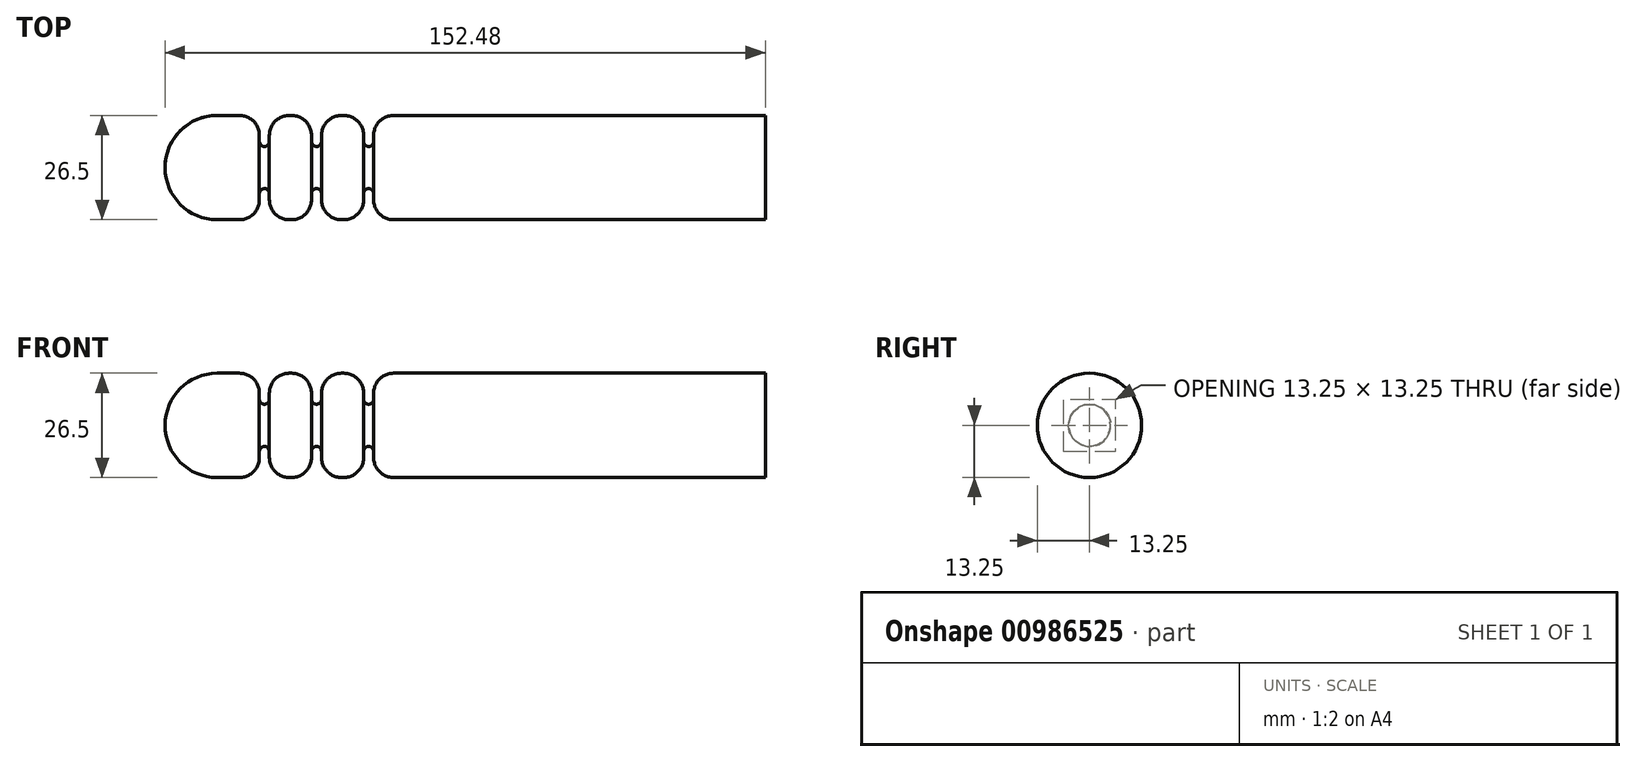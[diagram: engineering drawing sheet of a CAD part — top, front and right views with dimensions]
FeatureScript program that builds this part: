
annotation { "Feature Type Name" : "Feature", "Feature Type Description" : "" }
export const myFeature = defineFeature(function(context is Context, id is Id, definition is map)
    precondition{}
    {
        {
            var Q0;
            Q0=qCreatedBy(makeId("Top.planeOp"),FACE);
            var sketch = newSketch(context, id + "F0", { "sketchPlane" : qUnion([Q0])});
            skLineSegment(sketch, "E0", {"start": v(-75.98, 0) * mm, "end": v(76.5, 0) * mm, "construction": true});
            skCircle(sketch, "E1", {"center": v(-62.74, 0) * mm, "radius": 13.25 * mm, "construction": true});
            skCircle(sketch, "E2", {"center": v(-49.49, 0) * mm, "radius": 13.25 * mm, "construction": true});
            skLineSegment(sketch, "E3", {"start": v(-62.74, 0) * mm, "end": v(-62.74, 31.04) * mm, "construction": true});
            skLineSegment(sketch, "E4", {"start": v(-62.74, 31.04) * mm, "end": v(-62.74, 13.25) * mm, "construction": true});
            skLineSegment(sketch, "E5", {"start": v(-62.74, 13.25) * mm, "end": v(75.2, 13.25) * mm, "construction": true});
            skCircle(sketch, "E6", {"center": v(-36.24, 0) * mm, "radius": 13.25 * mm, "construction": true});
            skCircle(sketch, "E7", {"center": v(-22.99, 0) * mm, "radius": 13.25 * mm, "construction": true});
            skLineSegment(sketch, "E8", {"start": v(-49.49, 13.25) * mm, "end": v(-49.49, 0) * mm, "construction": true});
            skLineSegment(sketch, "E9", {"start": v(-36.24, 13.25) * mm, "end": v(-36.24, 0) * mm, "construction": true});
            skLineSegment(sketch, "E10", {"start": v(-22.99, 13.25) * mm, "end": v(-22.99, 0) * mm, "construction": true});
            skArc(sketch, "E11", {"start": v(-62.74, 13.25) * mm, "mid": v(-72.1, 9.37) * mm, "end": v(-75.98, 0) * mm});
            skLineSegment(sketch, "E12.0", {"start": v(-52.03, 13.25) * mm, "end": v(-52.03, 0) * mm, "construction": true});
            skLineSegment(sketch, "E13", {"start": v(-62.74, 5.36) * mm, "end": v(-3.86, 5.36) * mm, "construction": true});
            skLineSegment(sketch, "E14", {"start": v(-3.86, 5.36) * mm, "end": v(-4.4, 5.5) * mm, "construction": true});
            skLineSegment(sketch, "E15.0", {"start": v(-38.78, 13.25) * mm, "end": v(-38.78, 0) * mm, "construction": true});
            skLineSegment(sketch, "E16.0", {"start": v(-25.53, 13.25) * mm, "end": v(-25.53, 0) * mm, "construction": true});
            skLineSegment(sketch, "E17", {"start": v(-62.74, 13.25) * mm, "end": v(-52.03, 13.25) * mm});
            skLineSegment(sketch, "E18", {"start": v(-52.03, 5.36) * mm, "end": v(-52.03, 13.25) * mm});
            skLineSegment(sketch, "E19", {"start": v(-52.03, 5.36) * mm, "end": v(-49.49, 5.36) * mm});
            skLineSegment(sketch, "E20", {"start": v(-38.78, 5.36) * mm, "end": v(-38.78, 13.25) * mm});
            skLineSegment(sketch, "E21", {"start": v(-38.78, 13.25) * mm, "end": v(-49.49, 13.25) * mm});
            skLineSegment(sketch, "E22", {"start": v(-49.49, 13.25) * mm, "end": v(-49.49, 5.36) * mm});
            skLineSegment(sketch, "E23", {"start": v(-38.78, 5.36) * mm, "end": v(-36.24, 5.36) * mm});
            skLineSegment(sketch, "E24", {"start": v(-36.24, 13.25) * mm, "end": v(-36.24, 5.36) * mm});
            skLineSegment(sketch, "E25", {"start": v(-36.24, 13.25) * mm, "end": v(-25.53, 13.25) * mm});
            skLineSegment(sketch, "E26", {"start": v(-25.53, 13.25) * mm, "end": v(-25.53, 5.36) * mm});
            skLineSegment(sketch, "E27", {"start": v(-22.99, 5.36) * mm, "end": v(-25.53, 5.36) * mm});
            skLineSegment(sketch, "E28", {"start": v(-22.99, 5.36) * mm, "end": v(-22.99, 13.25) * mm});
            skLineSegment(sketch, "E29", {"start": v(-22.99, 13.25) * mm, "end": v(76.5, 13.25) * mm});
            skLineSegment(sketch, "E30", {"start": v(76.5, 0) * mm, "end": v(76.5, 13.25) * mm});
            skLineSegment(sketch, "E31", {"start": v(76.5, 0) * mm, "end": v(-75.98, 0) * mm});
            skSolve(sketch);
        }
        {
            var Q0;
            Q0=makeQuery(id+"F0.imprint","IMPRINT",FACE,{"disambiguationData":[TD([[makeQuery(id+"F0.imprint","IMPRINT",EDGE,{"derivedFrom":sQuery(id+"F0.wireOp",EDGE,"E11")}),1.0]])]});
            var Q1;
            Q1=sQuery(id+"F0.wireOp",EDGE,"E31");
            revolve(context, id + "F1", {"surfaceOperationType" : NewSurfaceOperationType.NEW, "entities" : qUnion([Q0]), "axis" : qUnion([Q1]), "revolveType" : RevolveType.FULL});
        }
        {
            var Q0;
            Q0=makeQuery(id+"F1.opRevolve","SWEPT_EDGE",EDGE,{"disambiguationData":[OSD([sQuery(id+"F0.wireOp",EDGE,"E17"),sQuery(id+"F0.wireOp",EDGE,"E18")])]});
            var Q1;
            Q1=makeQuery(id+"F1.opRevolve","SWEPT_EDGE",EDGE,{"disambiguationData":[OSD([sQuery(id+"F0.wireOp",EDGE,"E21"),sQuery(id+"F0.wireOp",EDGE,"E22")])]});
            var Q2;
            Q2=makeQuery(id+"F1.opRevolve","SWEPT_EDGE",EDGE,{"disambiguationData":[OSD([sQuery(id+"F0.wireOp",EDGE,"E20"),sQuery(id+"F0.wireOp",EDGE,"E21")])]});
            var Q3;
            Q3=makeQuery(id+"F1.opRevolve","SWEPT_EDGE",EDGE,{"disambiguationData":[OSD([sQuery(id+"F0.wireOp",EDGE,"E24"),sQuery(id+"F0.wireOp",EDGE,"E25")])]});
            var Q4;
            Q4=makeQuery(id+"F1.opRevolve","SWEPT_EDGE",EDGE,{"disambiguationData":[OSD([sQuery(id+"F0.wireOp",EDGE,"E25"),sQuery(id+"F0.wireOp",EDGE,"E26")])]});
            var Q5;
            Q5=makeQuery(id+"F1.opRevolve","SWEPT_EDGE",EDGE,{"disambiguationData":[OSD([sQuery(id+"F0.wireOp",EDGE,"E28"),sQuery(id+"F0.wireOp",EDGE,"E29")])]});
            fillet(context, id + "F2", {"entities" : qUnion([Q0, Q1, Q2, Q3, Q4, Q5]), "radius" : 5.08 * mm, "tangentPropagation" : true, "allowEdgeOverflow" : false});
        }
        {
            var Q0;
            Q0=makeQuery(id+"F1.opRevolve","SWEPT_EDGE",EDGE,{"disambiguationData":[OSD([sQuery(id+"F0.wireOp",EDGE,"E19"),sQuery(id+"F0.wireOp",EDGE,"E22")])]});
            var Q1;
            Q1=makeQuery(id+"F1.opRevolve","SWEPT_EDGE",EDGE,{"disambiguationData":[OSD([sQuery(id+"F0.wireOp",EDGE,"E18"),sQuery(id+"F0.wireOp",EDGE,"E19")])]});
            var Q2;
            Q2=makeQuery(id+"F1.opRevolve","SWEPT_EDGE",EDGE,{"disambiguationData":[OSD([sQuery(id+"F0.wireOp",EDGE,"E23"),sQuery(id+"F0.wireOp",EDGE,"E24")])]});
            var Q3;
            Q3=makeQuery(id+"F1.opRevolve","SWEPT_EDGE",EDGE,{"disambiguationData":[OSD([sQuery(id+"F0.wireOp",EDGE,"E20"),sQuery(id+"F0.wireOp",EDGE,"E23")])]});
            var Q4;
            Q4=makeQuery(id+"F1.opRevolve","SWEPT_EDGE",EDGE,{"disambiguationData":[OSD([sQuery(id+"F0.wireOp",EDGE,"E26"),sQuery(id+"F0.wireOp",EDGE,"E27")])]});
            var Q5;
            Q5=makeQuery(id+"F1.opRevolve","SWEPT_EDGE",EDGE,{"disambiguationData":[OSD([sQuery(id+"F0.wireOp",EDGE,"E27"),sQuery(id+"F0.wireOp",EDGE,"E28")])]});
            fillet(context, id + "F3", {"entities" : qUnion([Q0, Q1, Q2, Q3, Q4, Q5]), "radius" : 1.27 * mm, "tangentPropagation" : true, "allowEdgeOverflow" : false});
        }
    });
